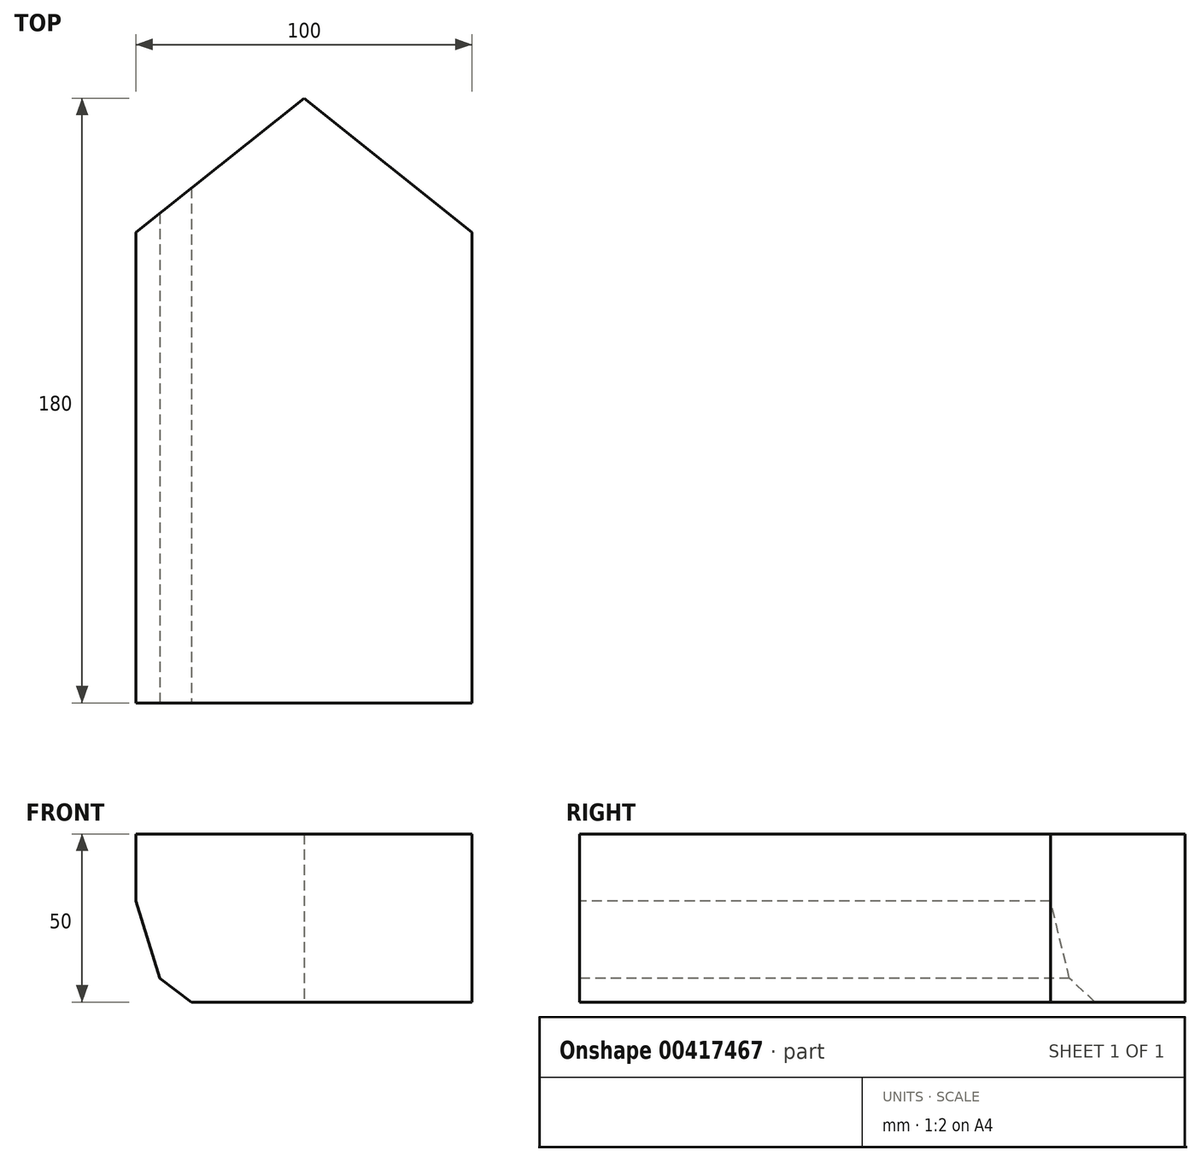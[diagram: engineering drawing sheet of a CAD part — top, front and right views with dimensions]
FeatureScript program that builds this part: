
annotation { "Feature Type Name" : "Feature", "Feature Type Description" : "" }
export const myFeature = defineFeature(function(context is Context, id is Id, definition is map)
    precondition{}
    {
        {
            var Q0;
            Q0=qCreatedBy(makeId("Top.planeOp"),FACE);
            var sketch = newSketch(context, id + "F0", { "sketchPlane" : qUnion([Q0])});
            skLineSegment(sketch, "E0.top", {"start": v(50, -70) * mm, "end": v(-50, -70) * mm});
            skLineSegment(sketch, "E0.left", {"start": v(50, 70) * mm, "end": v(50, -70) * mm});
            skLineSegment(sketch, "E0.right", {"start": v(-50, 70) * mm, "end": v(-50, -70) * mm});
            skPoint(sketch, "E0.middle", {"position": v(0, 0) * mm});
            skLineSegment(sketch, "E1", {"start": v(-50, 70) * mm, "end": v(0, 110) * mm});
            skLineSegment(sketch, "E2", {"start": v(0, 110) * mm, "end": v(50, 70) * mm});
            skSolve(sketch);
        }
        {
            var Q0;
            Q0 = qSketchRegion(id + "F0", true);
            extrude(context, id + "F1", {"entities" : qUnion([Q0]), "depth" : 50 * mm});
        }
        {
            var Q0;
            Q0=makeQuery(id+"F1.opExtrude","SWEPT_FACE",FACE,{"disambiguationData":[OSD([sQuery(id+"F0.wireOp",EDGE,"E0.top")])]});
            var sketch = newSketch(context, id + "F2", { "sketchPlane" : qUnion([Q0])});
            skLineSegment(sketch, "E3", {"start": v(-33.5, 0) * mm, "end": v(33.5, 0) * mm});
            skLineSegment(sketch, "E4", {"start": v(-42.93, 7.07) * mm, "end": v(-33.5, 0) * mm});
            skPoint(sketch, "E5", {"position": v(-50, 30) * mm});
            skLineSegment(sketch, "E6", {"start": v(-50, 30) * mm, "end": v(-42.93, 7.07) * mm});
            skSolve(sketch);
        }
        {
            var Q0;
            {var subQ0=sQuery(id+"F2.wireOp",EDGE,"E4");Q0=makeQuery(id+"F2.imprint","IMPRINT",FACE,{"disambiguationData":[TD([[makeQuery(id+"F2.imprint","IMPRINT",EDGE,{"derivedFrom":subQ0}),-1.0]])]});}
            extrude(context, id + "F3", {"entities" : qUnion([Q0]), "operationType" : NewBodyOperationType.REMOVE, "oppositeDirection" : true, "depth" : 180 * mm});
        }
    });
